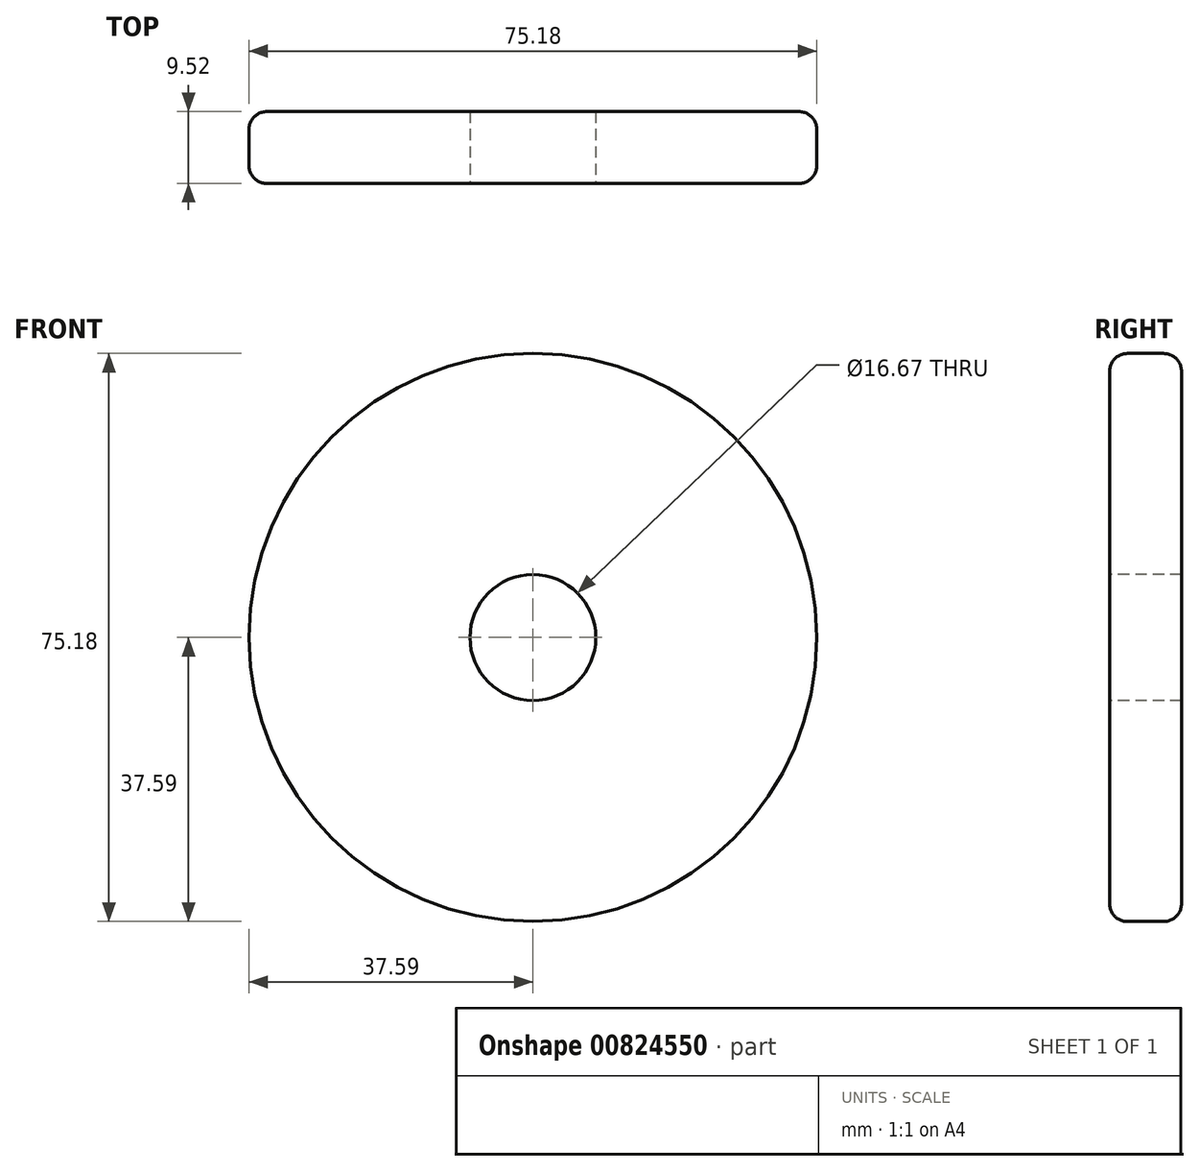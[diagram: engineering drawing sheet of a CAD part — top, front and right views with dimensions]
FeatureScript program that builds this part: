
annotation { "Feature Type Name" : "Feature", "Feature Type Description" : "" }
export const myFeature = defineFeature(function(context is Context, id is Id, definition is map)
    precondition{}
    {
        {
            var Q0;
            Q0=qCreatedBy(makeId("Front.planeOp"),FACE);
            var sketch = newSketch(context, id + "F0", { "sketchPlane" : qUnion([Q0])});
            skCircle(sketch, "E0", {"center": v(0, 0) * mm, "radius": 37.6 * mm});
            skSolve(sketch);
        }
        {
            var Q0;
            Q0=makeQuery(id+"F0.imprint","IMPRINT",FACE,{"disambiguationData":[TD([[makeQuery(id+"F0.imprint","IMPRINT",EDGE,{"derivedFrom":sQuery(id+"F0.wireOp",EDGE,"E0")}),1.0]])]});
            extrude(context, id + "F1", {"entities" : qUnion([Q0]), "endBound" : BoundingType.SYMMETRIC, "depth" : 9.52 * mm, "offsetDistance" : 25.4 * mm});
        }
        {
            var Q0;
            Q0=makeQuery(id+"F1.opExtrude","CAP_FACE",FACE,{"disambiguationData":[OSD([sQuery(id+"F0.wireOp",EDGE,"E0")])],"isStart":false});
            var sketch = newSketch(context, id + "F2", { "sketchPlane" : qUnion([Q0])});
            skPoint(sketch, "E1", {"position": v(0, 0) * mm});
            skSolve(sketch);
        }
        {
            var Q0;
            Q0=sQuery(id+"F2.wireOp",VERTEX,"E1");
            var Q1;
            Q1=makeQuery(id+"F1.opExtrude","SWEPT_BODY",BODY,{"disambiguationData":[OSD([sQuery(id+"F0.wireOp",EDGE,"E0")])]});
            hole(context, id + "F3", {"style" : HoleStyle.SIMPLE, "endStyle" : HoleEndStyle.THROUGH, "standardTappedOrClearance" : lookupTablePath({ "standard" : "ANSI", "fit" : "Normal (ASME)", "size" : "5/8", "type" : "Clearance" }), "standardBlindInLast" : lookupTablePath({ "fit" : "Free", "standard" : "ANSI", "size" : "5/8", "type" : "Clearance" }), "holeDiameter" : 16.67 * mm, "majorDiameter" : 6.35 * mm, "isTappedThrough" : true, "tappedDepth" : 34.3 * mm, "tapClearance" : 3, "startFromSketch" : true, "locations" : qUnion([Q0]), "scope" : qUnion([Q1])});
        }
        {
            var Q0;
            Q0=makeQuery(id+"F1.opExtrude","CAP_EDGE",EDGE,{"disambiguationData":[OSD([sQuery(id+"F0.wireOp",EDGE,"E0")])],"isStart":false});
            var Q1;
            Q1=makeQuery(id+"F1.opExtrude","CAP_EDGE",EDGE,{"disambiguationData":[OSD([sQuery(id+"F0.wireOp",EDGE,"E0")])],"isStart":true});
            fillet(context, id + "F4", {"entities" : qUnion([Q0, Q1]), "radius" : 2.36 * mm, "tangentPropagation" : true, "allowEdgeOverflow" : false});
        }
    });
